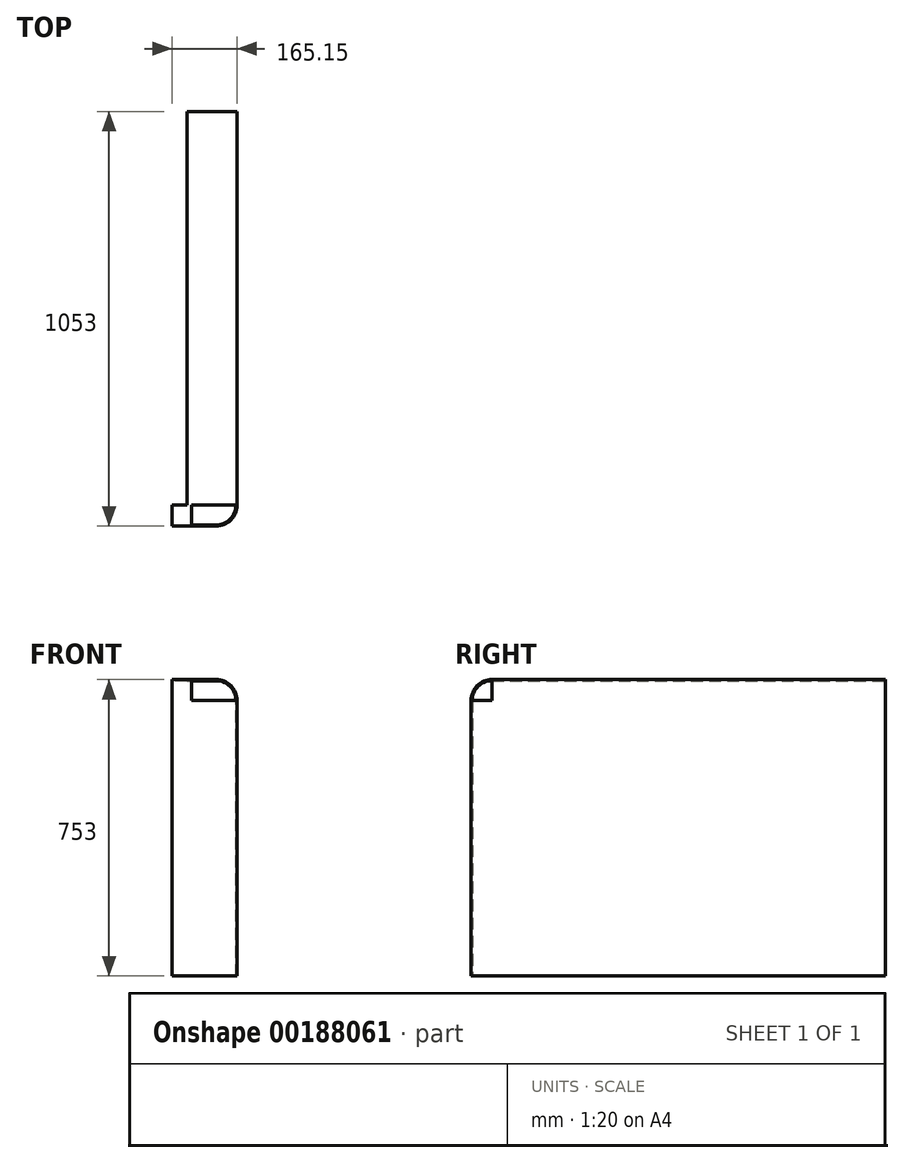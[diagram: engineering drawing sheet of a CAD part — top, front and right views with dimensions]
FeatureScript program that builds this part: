
annotation { "Feature Type Name" : "Feature", "Feature Type Description" : "" }
export const myFeature = defineFeature(function(context is Context, id is Id, definition is map)
    precondition{}
    {
        {
            var Q0;
            Q0=qCreatedBy(makeId("Right.planeOp"),FACE);
            var sketch = newSketch(context, id + "F0", { "sketchPlane" : qUnion([Q0])});
            skLineSegment(sketch, "E0.bottom", {"start": v(500, -350) * mm, "end": v(-500, -350) * mm});
            skLineSegment(sketch, "E0.top", {"start": v(500, 350) * mm, "end": v(-500, 350) * mm});
            skLineSegment(sketch, "E0.left", {"start": v(500, -350) * mm, "end": v(500, 350) * mm});
            skLineSegment(sketch, "E0.right", {"start": v(-500, -350) * mm, "end": v(-500, 350) * mm});
            skPoint(sketch, "E0.middle", {"position": v(0, 0) * mm});
            skSolve(sketch);
        }
        {
            var Q0;
            Q0 = qSketchRegion(id + "F0", true);
            extrude(context, id + "F1", {"entities" : qUnion([Q0]), "depth" : 3 * mm});
        }
        {
            var Q0;
            Q0=makeQuery(id+"F1.opExtrude","SWEPT_FACE",FACE,{"disambiguationData":[OSD([sQuery(id+"F0.wireOp",EDGE,"E0.left")])]});
            var sketch = newSketch(context, id + "F2", { "sketchPlane" : qUnion([Q0])});
            skArc(sketch, "E1", {"start": v(50, 403) * mm, "mid": v(12.52, 387.48) * mm, "end": v(-3, 350) * mm});
            skLineSegment(sketch, "E2", {"start": v(50, 403) * mm, "end": v(123.8, 403) * mm});
            skLineSegment(sketch, "E3", {"start": v(-3, 350) * mm, "end": v(50, 350) * mm, "construction": true});
            skLineSegment(sketch, "E4", {"start": v(50, 350) * mm, "end": v(50, 376.69) * mm, "construction": true});
            skLineSegment(sketch, "E5", {"start": v(123.8, 403) * mm, "end": v(123.8, 400) * mm});
            skLineSegment(sketch, "E6", {"start": v(123.8, 400) * mm, "end": v(50, 400) * mm});
            skArc(sketch, "E7", {"start": v(50, 400) * mm, "mid": v(14.64, 385.36) * mm, "end": v(0, 350) * mm});
            skLineSegment(sketch, "E8", {"start": v(0, 350) * mm, "end": v(50, 350) * mm, "construction": true});
            skLineSegment(sketch, "E9", {"start": v(50, 345.34) * mm, "end": v(50, 350) * mm, "construction": true});
            skLineSegment(sketch, "E10", {"start": v(-3, 350) * mm, "end": v(0, 350) * mm});
            skSolve(sketch);
        }
        {
            var Q0;
            Q0 = qSketchRegion(id + "F2", true);
            extrude(context, id + "F3", {"entities" : qUnion([Q0]), "operationType" : NewBodyOperationType.ADD, "oppositeDirection" : true, "depth" : 1000 * mm});
        }
        {
            var Q0;
            Q0=makeQuery(id+"F1.opExtrude","SWEPT_FACE",FACE,{"disambiguationData":[OSD([sQuery(id+"F0.wireOp",EDGE,"E0.bottom")])]});
            var sketch = newSketch(context, id + "F4", { "sketchPlane" : qUnion([Q0])});
            skArc(sketch, "E11.MirrorCS", {"start": v(-50, 550) * mm, "mid": v(-14.64, 535.36) * mm, "end": v(0, 500) * mm});
            skArc(sketch, "E12.MirrorCS", {"start": v(-50, 553) * mm, "mid": v(-12.52, 537.48) * mm, "end": v(3, 500) * mm});
            skLineSegment(sketch, "E13.MirrorCS", {"start": v(-50, 500) * mm, "end": v(-50, 550) * mm, "construction": true});
            skLineSegment(sketch, "E14", {"start": v(-50, 553) * mm, "end": v(-162.15, 553) * mm});
            skLineSegment(sketch, "E15", {"start": v(-162.15, 553) * mm, "end": v(-162.15, 550) * mm});
            skLineSegment(sketch, "E16", {"start": v(-162.15, 550) * mm, "end": v(-50, 550) * mm});
            skLineSegment(sketch, "E17", {"start": v(-50, 500) * mm, "end": v(244.82, 500) * mm, "construction": true});
            skLineSegment(sketch, "E18", {"start": v(0, 500) * mm, "end": v(3, 500) * mm});
            skSolve(sketch);
        }
        {
            var Q0;
            Q0 = qSketchRegion(id + "F4", true);
            extrude(context, id + "F5", {"entities" : qUnion([Q0]), "operationType" : NewBodyOperationType.ADD, "oppositeDirection" : true, "depth" : 700 * mm});
        }
        {
            var Q0;
            Q0=makeQuery(id+"F5.opExtrude","SWEPT_FACE",FACE,{"disambiguationData":[OSD([sQuery(id+"F4.wireOp",EDGE,"E15")])]});
            var sketch = newSketch(context, id + "F6", { "sketchPlane" : qUnion([Q0])});
            skArc(sketch, "E19.MirrorCS", {"start": v(500, 400) * mm, "mid": v(535.36, 385.36) * mm, "end": v(550, 350) * mm});
            skArc(sketch, "E20.MirrorCS", {"start": v(500, 403) * mm, "mid": v(537.48, 387.48) * mm, "end": v(553, 350) * mm});
            skLineSegment(sketch, "E21.MirrorCS", {"start": v(500, 350) * mm, "end": v(500, 393.06) * mm, "construction": true});
            skLineSegment(sketch, "E22.MirrorCS", {"start": v(550, 350) * mm, "end": v(500, 350) * mm, "construction": true});
            skLineSegment(sketch, "E23", {"start": v(550, 350) * mm, "end": v(553, 350) * mm});
            skLineSegment(sketch, "E24", {"start": v(500, 403) * mm, "end": v(500, 400) * mm});
            skSolve(sketch);
        }
        {
            var Q0;
            Q0 = qSketchRegion(id + "F6", true);
            extrude(context, id + "F7", {"entities" : qUnion([Q0]), "operationType" : NewBodyOperationType.ADD, "oppositeDirection" : true, "depth" : 50 * mm});
        }
    });
